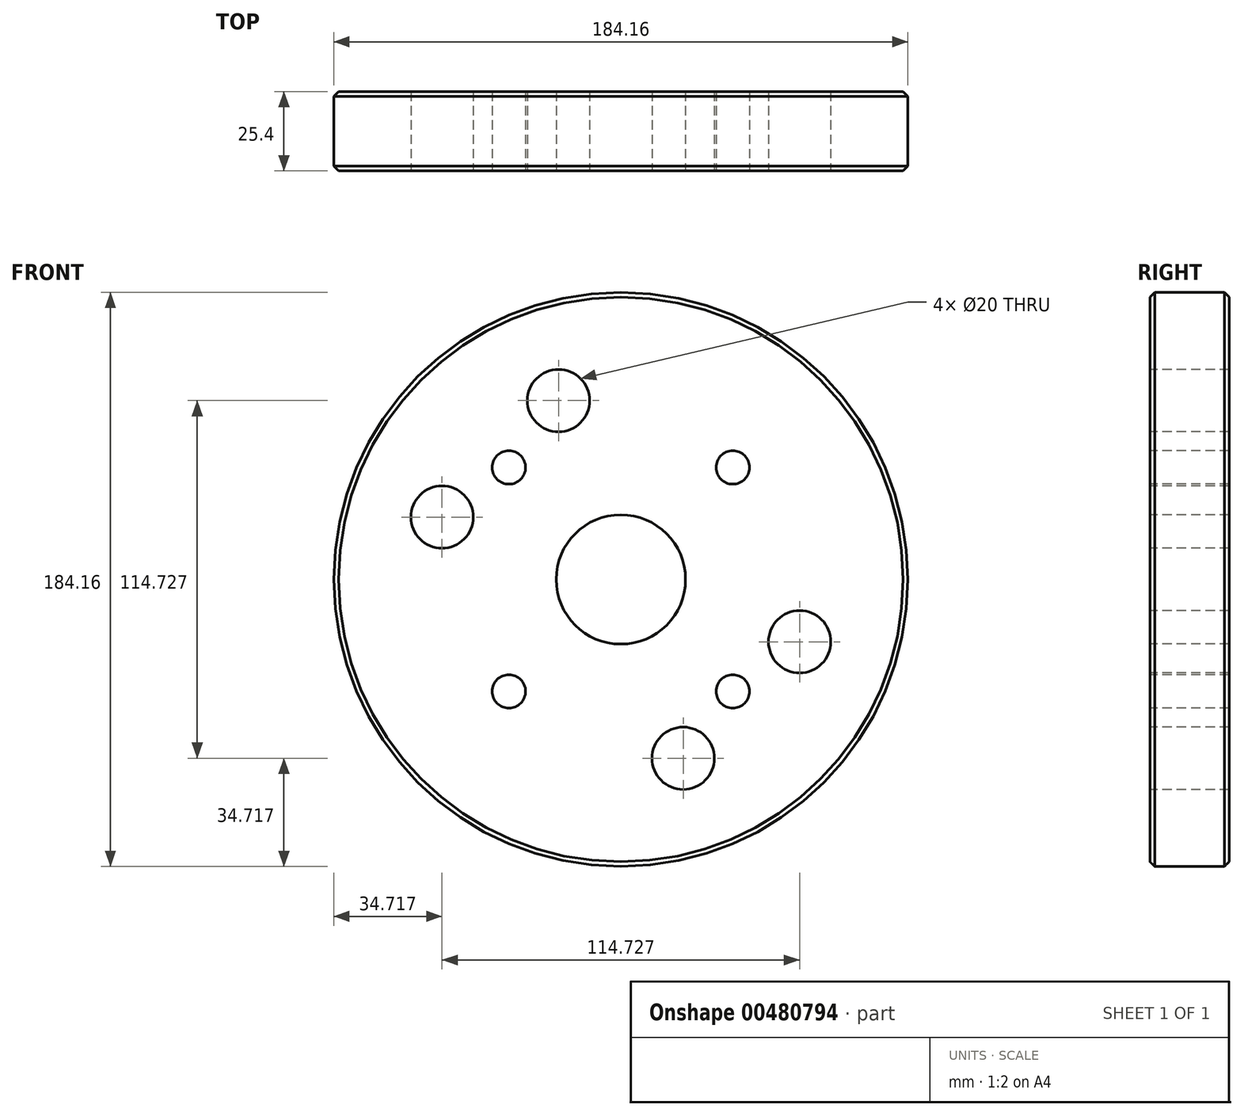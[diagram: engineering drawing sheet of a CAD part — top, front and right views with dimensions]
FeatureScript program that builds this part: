
annotation { "Feature Type Name" : "Feature", "Feature Type Description" : "" }
export const myFeature = defineFeature(function(context is Context, id is Id, definition is map)
    precondition{}
    {
        {
            var Q0;
            Q0=qCreatedBy(makeId("Front.planeOp"),FACE);
            var sketch = newSketch(context, id + "F0", { "sketchPlane" : qUnion([Q0])});
            skCircle(sketch, "E0", {"center": v(0, 0) * mm, "radius": 92.08 * mm});
            skCircle(sketch, "E1", {"center": v(0, 0) * mm, "radius": 20.75 * mm});
            skSolve(sketch);
        }
        {
            var Q0;
            Q0 = qSketchRegion(id + "F0", true);
            extrude(context, id + "F1", {"entities" : qUnion([Q0]), "oppositeDirection" : true, "depth" : 25.4 * mm});
        }
        {
            var Q0;
            Q0=makeQuery(id+"F1.opExtrude","CAP_FACE",FACE,{"disambiguationData":[OSD([sQuery(id+"F0.wireOp",EDGE,"E0"),sQuery(id+"F0.wireOp",EDGE,"E1")])],"isStart":true});
            var sketch = newSketch(context, id + "F2", { "sketchPlane" : qUnion([Q0])});
            skLineSegment(sketch, "E2", {"start": v(0, 92.08) * mm, "end": v(0, -92.08) * mm, "construction": true});
            skLineSegment(sketch, "E3.0", {"start": v(-10, 92.08) * mm, "end": v(-10, -92.08) * mm, "construction": true});
            skCircle(sketch, "E4", {"center": v(0, 0) * mm, "radius": 70.75 * mm, "construction": true});
            skCircle(sketch, "E5", {"center": v(0, 0) * mm, "radius": 30.64 * mm, "construction": true});
            skCircle(sketch, "E6", {"center": v(-20, 57.36) * mm, "radius": 10 * mm, "construction": true});
            skCircle(sketch, "E7", {"center": v(-20, 57.36) * mm, "radius": 10 * mm});
            skLineSegment(sketch, "E8", {"start": v(0, 0) * mm, "end": v(-99.85, 0) * mm, "construction": true});
            skLineSegment(sketch, "E9.0", {"start": v(0, 10) * mm, "end": v(-99.85, 10) * mm, "construction": true});
            skCircle(sketch, "E10", {"center": v(-57.36, 20) * mm, "radius": 10 * mm});
            skCircle(sketch, "E11.1.0", {"center": v(57.36, -20) * mm, "radius": 10 * mm});
            skCircle(sketch, "E11.1.1", {"center": v(20, -57.36) * mm, "radius": 10 * mm, "construction": true});
            skCircle(sketch, "E12", {"center": v(20, -57.36) * mm, "radius": 10 * mm});
            skSolve(sketch);
        }
        {
            var Q0;
            Q0=makeQuery(id+"F2.imprint","IMPRINT",FACE,{"disambiguationData":[TD([[makeQuery(id+"F2.imprint","IMPRINT",EDGE,{"derivedFrom":sQuery(id+"F2.wireOp",EDGE,"E10")}),1.0]])]});
            var Q1;
            Q1=makeQuery(id+"F2.imprint","IMPRINT",FACE,{"disambiguationData":[TD([[makeQuery(id+"F2.imprint","IMPRINT",EDGE,{"derivedFrom":sQuery(id+"F2.wireOp",EDGE,"E7")}),1.0]])]});
            var Q2;
            Q2=makeQuery(id+"F2.imprint","IMPRINT",FACE,{"disambiguationData":[TD([[makeQuery(id+"F2.imprint","IMPRINT",EDGE,{"derivedFrom":sQuery(id+"F2.wireOp",EDGE,"E11.1.0")}),1.0]])]});
            var Q3;
            Q3=makeQuery(id+"F2.imprint","IMPRINT",FACE,{"disambiguationData":[TD([[makeQuery(id+"F2.imprint","IMPRINT",EDGE,{"derivedFrom":sQuery(id+"F2.wireOp",EDGE,"E12")}),1.0]])]});
            extrude(context, id + "F3", {"entities" : qUnion([Q0, Q1, Q2, Q3]), "operationType" : NewBodyOperationType.REMOVE, "oppositeDirection" : true, "depth" : 25.4 * mm});
        }
        {
            var Q0;
            Q0=makeQuery(id+"F1.opExtrude","CAP_FACE",FACE,{"disambiguationData":[OSD([sQuery(id+"F0.wireOp",EDGE,"E0"),sQuery(id+"F0.wireOp",EDGE,"E1")])],"isStart":true});
            var sketch = newSketch(context, id + "F4", { "sketchPlane" : qUnion([Q0])});
            skCircle(sketch, "E13", {"center": v(0, 0) * mm, "radius": 50.8 * mm, "construction": true});
            skLineSegment(sketch, "E14", {"start": v(0, 0) * mm, "end": v(-35.92, 35.92) * mm, "construction": true});
            skPoint(sketch, "E15", {"position": v(-35.92, 35.92) * mm});
            skPoint(sketch, "E16.1.0", {"position": v(-35.92, -35.92) * mm});
            skPoint(sketch, "E16.2.0", {"position": v(35.92, -35.92) * mm});
            skPoint(sketch, "E16.3.0", {"position": v(35.92, 35.92) * mm});
            skSolve(sketch);
        }
        {
            var Q0;
            Q0=sQuery(id+"F4.wireOp",VERTEX,"E15");
            var Q1;
            Q1=sQuery(id+"F4.wireOp",VERTEX,"E16.3.0");
            var Q2;
            Q2=sQuery(id+"F4.wireOp",VERTEX,"E16.2.0");
            var Q3;
            Q3=sQuery(id+"F4.wireOp",VERTEX,"E16.1.0");
            var Q4;
            Q4=makeQuery(id+"F1.opExtrude","SWEPT_BODY",BODY,{"disambiguationData":[OSD([sQuery(id+"F0.wireOp",EDGE,"E0"),sQuery(id+"F0.wireOp",EDGE,"E1")])]});
            hole(context, id + "F5", {"style" : HoleStyle.SIMPLE, "endStyle" : HoleEndStyle.THROUGH, "standardTappedOrClearance" : lookupTablePath({ "standard" : "ANSI", "engagement" : "75%", "pitch" : "13 tpi", "size" : "1/2", "type" : "Tapped" }), "standardBlindInLast" : lookupTablePath({ "standard" : "ANSI", "engagement" : "75%", "pitch" : "13 tpi", "size" : "1/2", "type" : "Tapped" }), "holeDiameter" : 10.72 * mm, "showTappedDepth" : true, "tappedDepth" : 15.88 * mm, "tapClearance" : 3, "startFromSketch" : true, "locations" : qUnion([Q0, Q1, Q2, Q3]), "scope" : qUnion([Q4]), "majorDiameter" : 12.7 * mm});
        }
        {
            var Q0;
            Q0=makeQuery(id+"F1.opExtrude","SWEPT_FACE",FACE,{"disambiguationData":[OSD([sQuery(id+"F0.wireOp",EDGE,"E0")])]});
            chamfer(context, id + "F6", {"entities" : qUnion([Q0]), "width" : 1.52 * mm, "tangentPropagation" : true});
        }
    });
